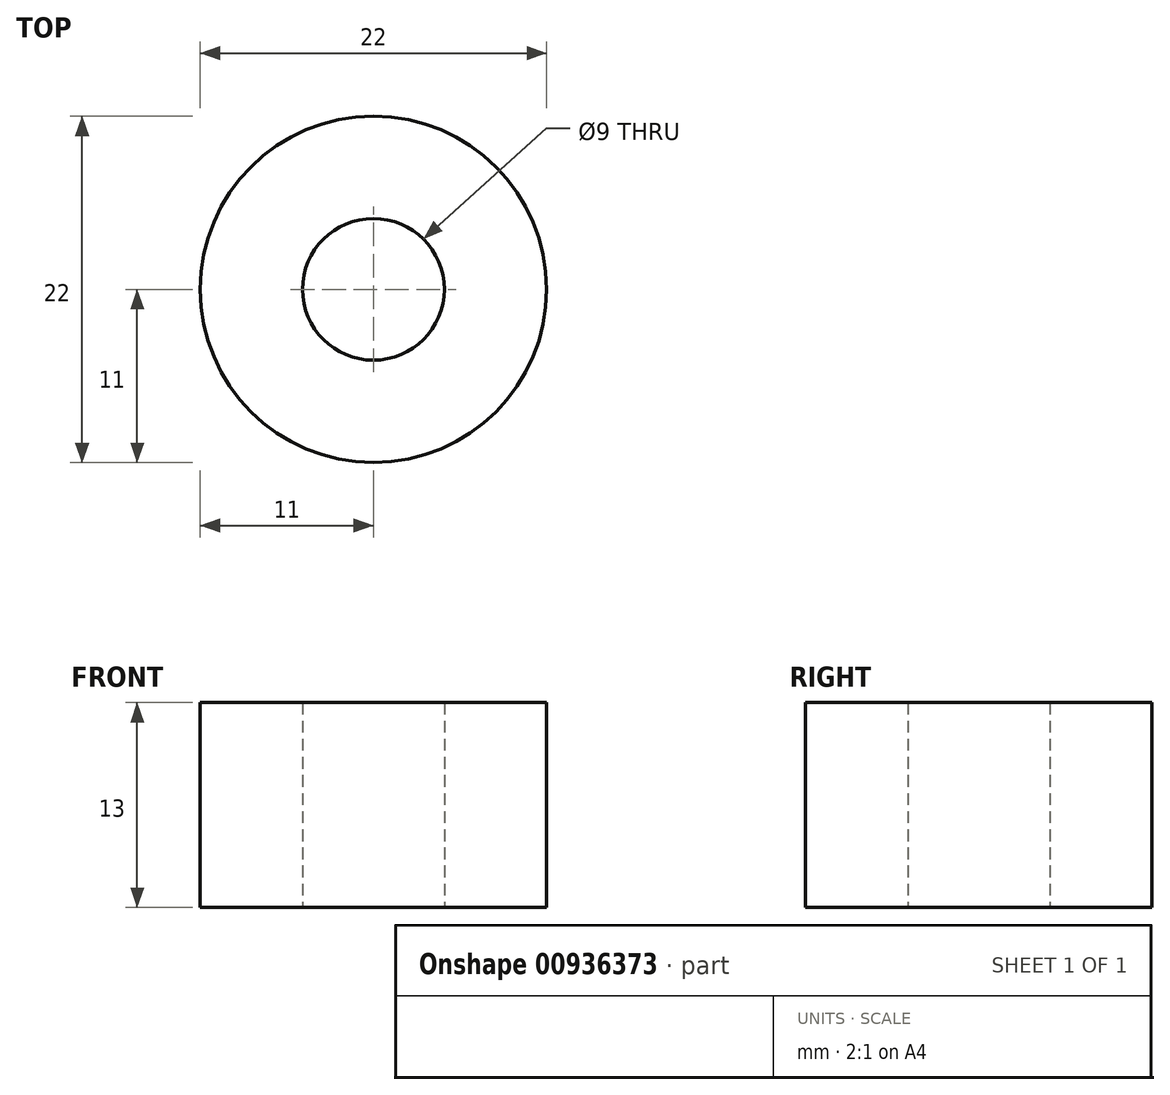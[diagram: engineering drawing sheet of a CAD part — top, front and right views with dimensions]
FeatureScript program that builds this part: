
annotation { "Feature Type Name" : "Feature", "Feature Type Description" : "" }
export const myFeature = defineFeature(function(context is Context, id is Id, definition is map)
    precondition{}
    {
        {
            var Q0;
            Q0=qCreatedBy(makeId("Top.planeOp"),FACE);
            var sketch = newSketch(context, id + "F0", { "sketchPlane" : qUnion([Q0])});
            skCircle(sketch, "E0", {"center": v(0, 0) * mm, "radius": 11 * mm});
            skCircle(sketch, "E1", {"center": v(0, 0) * mm, "radius": 4.5 * mm});
            skSolve(sketch);
        }
        {
            var Q0;
            Q0=makeQuery(id+"F0.imprint","IMPRINT",FACE,{"disambiguationData":[TD([[makeQuery(id+"F0.imprint","IMPRINT",EDGE,{"derivedFrom":sQuery(id+"F0.wireOp",EDGE,"E0")}),1.0]])]});
            extrude(context, id + "F1", {"entities" : qUnion([Q0]), "depth" : 13 * mm, "offsetDistance" : 25 * mm});
        }
    });
